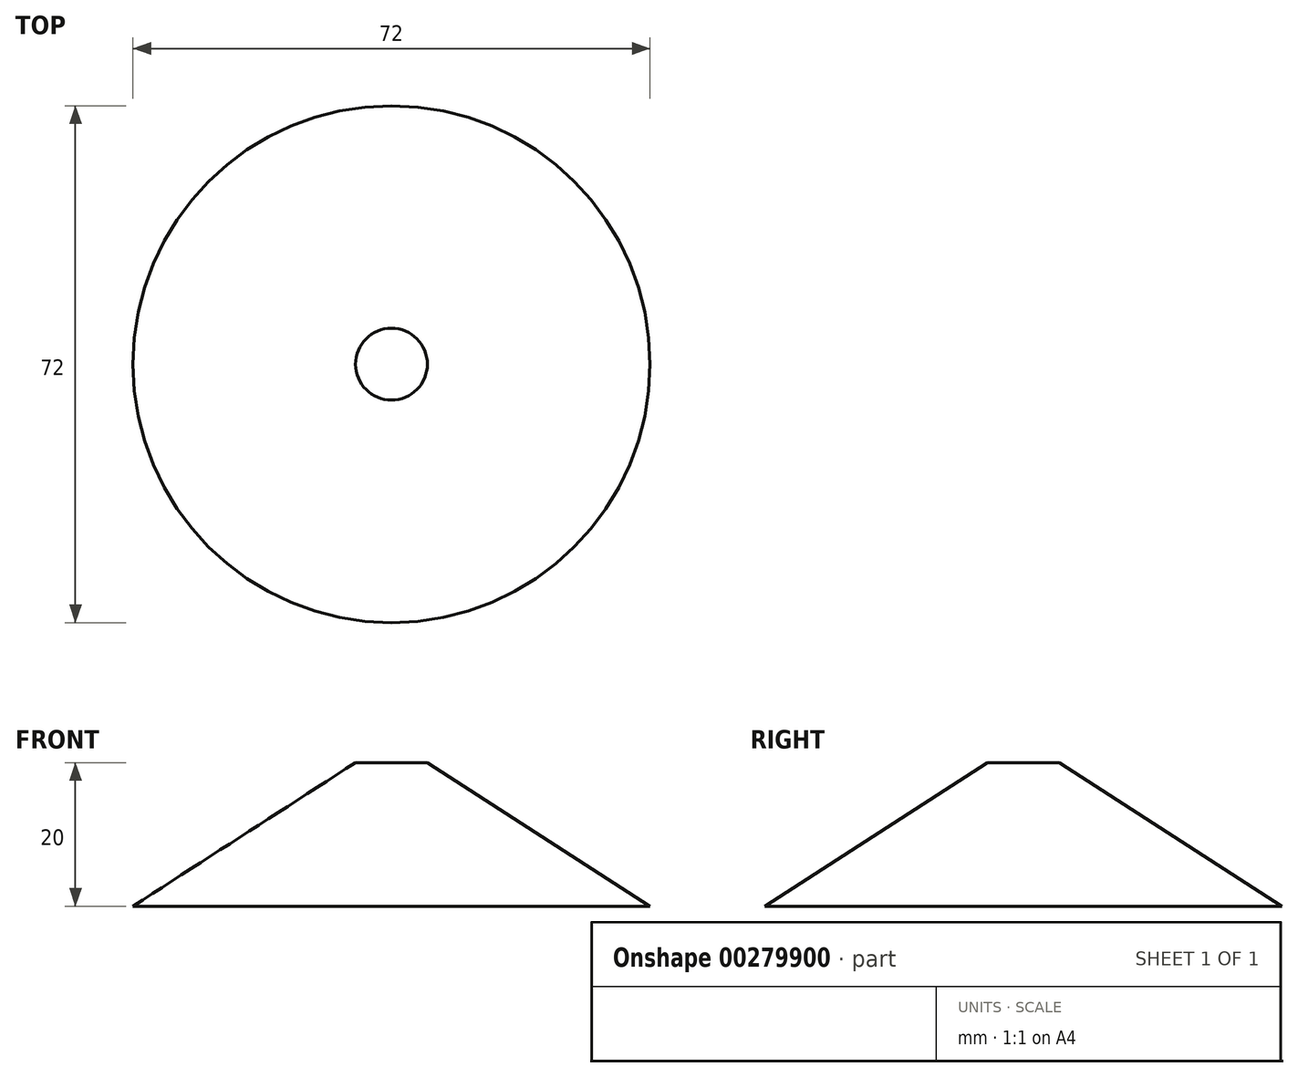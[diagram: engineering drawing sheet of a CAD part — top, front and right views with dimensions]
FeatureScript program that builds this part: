
annotation { "Feature Type Name" : "Feature", "Feature Type Description" : "" }
export const myFeature = defineFeature(function(context is Context, id is Id, definition is map)
    precondition{}
    {
        {
            var Q0;
            Q0=qCreatedBy(makeId("Front.planeOp"),FACE);
            var sketch = newSketch(context, id + "F0", { "sketchPlane" : qUnion([Q0])});
            skLineSegment(sketch, "E0", {"start": v(0, 0) * mm, "end": v(0, 25) * mm});
            skLineSegment(sketch, "E1", {"start": v(45, 0) * mm, "end": v(0, 0) * mm});
            skLineSegment(sketch, "E2", {"start": v(0, 0) * mm, "end": v(0, 20) * mm});
            skLineSegment(sketch, "E3", {"start": v(0, 0) * mm, "end": v(36, 0) * mm});
            skLineSegment(sketch, "E4", {"start": v(0, 25) * mm, "end": v(5, 25) * mm});
            skLineSegment(sketch, "E5", {"start": v(5, 25) * mm, "end": v(45, 0) * mm});
            skLineSegment(sketch, "E6", {"start": v(0, 20) * mm, "end": v(5, 20) * mm});
            skLineSegment(sketch, "E7", {"start": v(5, 20) * mm, "end": v(36, 0) * mm});
            skSolve(sketch);
        }
        {
            var Q0;
            Q0=makeQuery(id+"F0.imprint","IMPRINT",FACE,{"disambiguationData":[TD([[makeQuery(id+"F0.imprint","IMPRINT",EDGE,{"derivedFrom":sQuery(id+"F0.wireOp",EDGE,"E0")}),-1.0]])]});
            var Q1;
            Q1=sQuery(id+"F0.wireOp",EDGE,"E0");
            revolve(context, id + "F1", {"entities" : qUnion([Q0]), "axis" : qUnion([Q1]), "revolveType" : RevolveType.FULL});
        }
    });
